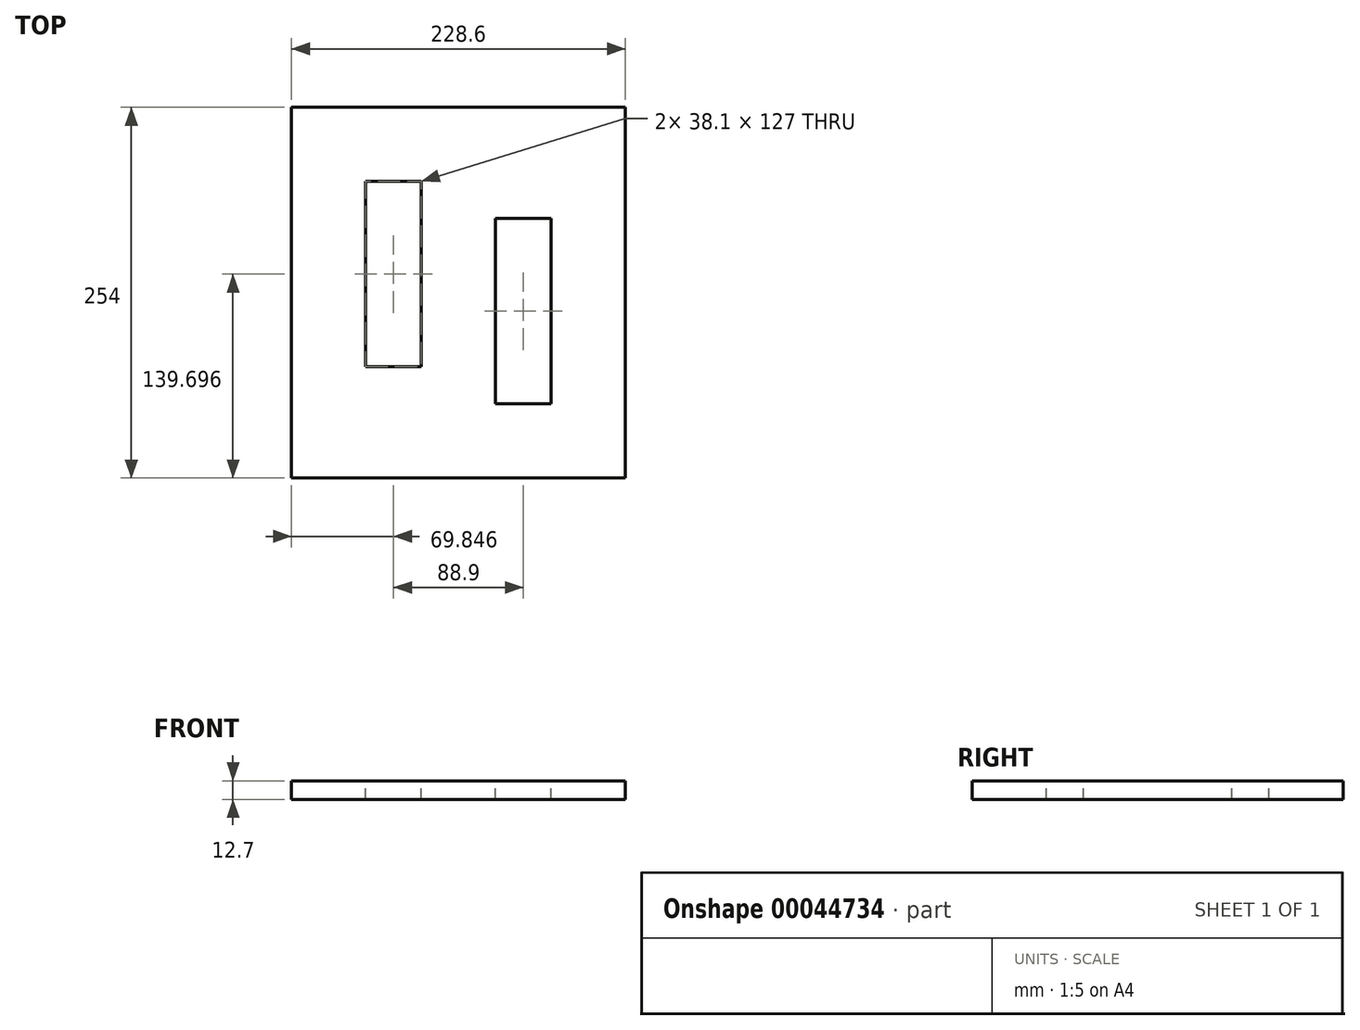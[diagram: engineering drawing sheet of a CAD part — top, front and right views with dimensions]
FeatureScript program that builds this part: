
annotation { "Feature Type Name" : "Feature", "Feature Type Description" : "" }
export const myFeature = defineFeature(function(context is Context, id is Id, definition is map)
    precondition{}
    {
        {
            var Q0;
            Q0=qCreatedBy(makeId("Top.planeOp"),FACE);
            var sketch = newSketch(context, id + "F0", { "sketchPlane" : qUnion([Q0])});
            skLineSegment(sketch, "E0.bottom", {"start": v(-108.73, -87.24) * mm, "end": v(119.87, -87.24) * mm});
            skLineSegment(sketch, "E0.top", {"start": v(-108.73, 166.76) * mm, "end": v(119.87, 166.76) * mm});
            skLineSegment(sketch, "E0.left", {"start": v(-108.73, -87.24) * mm, "end": v(-108.73, 166.76) * mm});
            skLineSegment(sketch, "E0.right", {"start": v(119.87, -87.24) * mm, "end": v(119.87, 166.76) * mm});
            skSolve(sketch);
        }
        {
            var Q0;
            Q0=qSketchRegion(id+"F0",true);
            var Q1;
            Q1=sQuery(id+"F0.wireOp",EDGE,"E0.bottom");
            var Q2;
            Q2=sQuery(id+"F0.wireOp",EDGE,"E0.right");
            var Q3;
            Q3=sQuery(id+"F0.wireOp",EDGE,"E0.left");
            var Q4;
            Q4=sQuery(id+"F0.wireOp",EDGE,"E0.top");
            extrude(context, id + "F1", {"entities" : qUnion([Q0]), "surfaceEntities" : qUnion([Q1, Q2, Q3, Q4]), "depth" : 12.7 * mm});
        }
        {
            var Q0;
            Q0=makeQuery(id+"F1.opExtrude","CAP_FACE",FACE,{"disambiguationData":[OSD([sQuery(id+"F0.wireOp",EDGE,"E0.bottom"),sQuery(id+"F0.wireOp",EDGE,"E0.top"),sQuery(id+"F0.wireOp",EDGE,"E0.left"),sQuery(id+"F0.wireOp",EDGE,"E0.right")])],"isStart":false});
            var sketch = newSketch(context, id + "F2", { "sketchPlane" : qUnion([Q0])});
            skLineSegment(sketch, "E1.rect.bottom", {"start": v(-19.83, -11.04) * mm, "end": v(-57.93, -11.04) * mm});
            skLineSegment(sketch, "E1.rect.top", {"start": v(-19.83, 115.96) * mm, "end": v(-57.93, 115.96) * mm});
            skLineSegment(sketch, "E1.rect.left", {"start": v(-19.83, -11.04) * mm, "end": v(-19.83, 115.96) * mm});
            skLineSegment(sketch, "E1.rect.right", {"start": v(-57.93, -11.04) * mm, "end": v(-57.93, 115.96) * mm});
            skPoint(sketch, "E1.rect.middle", {"position": v(-38.88, 52.46) * mm});
            skLineSegment(sketch, "E2.rect.bottom", {"start": v(69.07, -36.44) * mm, "end": v(30.97, -36.44) * mm});
            skLineSegment(sketch, "E2.rect.top", {"start": v(69.07, 90.56) * mm, "end": v(30.97, 90.56) * mm});
            skLineSegment(sketch, "E2.rect.left", {"start": v(69.07, -36.44) * mm, "end": v(69.07, 90.56) * mm});
            skLineSegment(sketch, "E2.rect.right", {"start": v(30.97, -36.44) * mm, "end": v(30.97, 90.56) * mm});
            skPoint(sketch, "E2.rect.middle", {"position": v(50.02, 27.06) * mm});
            skSolve(sketch);
        }
        {
            var Q0;
            Q0=makeQuery(id+"F2.imprint","IMPRINT",FACE,{"disambiguationData":[TD([[makeQuery(id+"F2.imprint","IMPRINT",EDGE,{"derivedFrom":sQuery(id+"F2.wireOp",EDGE,"E1.rect.bottom")}),-1.0]])]});
            var Q1;
            Q1=makeQuery(id+"F2.imprint","IMPRINT",FACE,{"disambiguationData":[TD([[makeQuery(id+"F2.imprint","IMPRINT",EDGE,{"derivedFrom":sQuery(id+"F2.wireOp",EDGE,"E2.rect.bottom")}),-1.0]])]});
            extrude(context, id + "F3", {"entities" : qUnion([Q0, Q1]), "operationType" : NewBodyOperationType.REMOVE, "oppositeDirection" : true, "depth" : 12.7 * mm});
        }
    });
